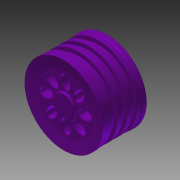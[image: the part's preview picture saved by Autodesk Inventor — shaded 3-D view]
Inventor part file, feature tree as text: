
AUTODESK INVENTOR PART (.ipt)
format: ipt  version: 2014 (Build 180170000, 170)  size: 219,648 bytes
history: native  units: mm
features: sketch x4, other x1, revolve x1, plane x1, hole x1, extrude x1, pattern_circular x1
ambient origin geometry x8: Origin, YZ Plane, XZ Plane, XY Plane, X Axis, Y Axis, Z Axis, Center Point
bodies: Body1 (feature_tree)
feature tree (10):
  other  "Sólido1"
  revolve  "Revolución1"  [1 undecoded]
  sketch  "Boceto2"  dims[d7=32.0mm d8=10.0mm]
  plane  "Plano de trabajo1"
  hole  "Hole1"  [1 undecoded]
  extrude  "Extrusión1"  Depth=44.5mm
  pattern_circular  "Patrón circular1"  [2 undecoded]
  sketch  "Boceto1"  dims[d1=45.0mm d3=12.217305mm d4=12.217305mm d6=25.0mm]
  sketch  "Boceto3"  dims[d10=90.0deg d17=44.5mm]
  sketch  "Boceto4"  dims[d18=44.5mm d23=0.5mm d24=0.5mm d31=5.0mm d32=8.0mm d33=3.0mm d34=1.567mm d35=6.0mm d36=4.0mm d37=2.0mm d38=90.0deg d39=8.0mm d40=20.594885mm d41=30.0mm d42=25.0mm d45=29.670597mm d46=44.0mm d55=43.5mm d56=4.0mm d60=4.0mm d61=3.0mm d62=2.625mm d63=2.625mm d64=2.625mm d65=2.0mm d66=44.0mm d67=44.0mm d68=44.0mm d69=44.0mm d70=2.1mm d73=4.0mm d74=2.5mm d76=10.0mm d77=0.0mm d78=80.0mm d79=360.0deg]
note: 4 required parameter values undecoded (feature->parameter linkage not recoverable at this tier; creation-order binding heuristic only, values carry confidence <= 0.55)